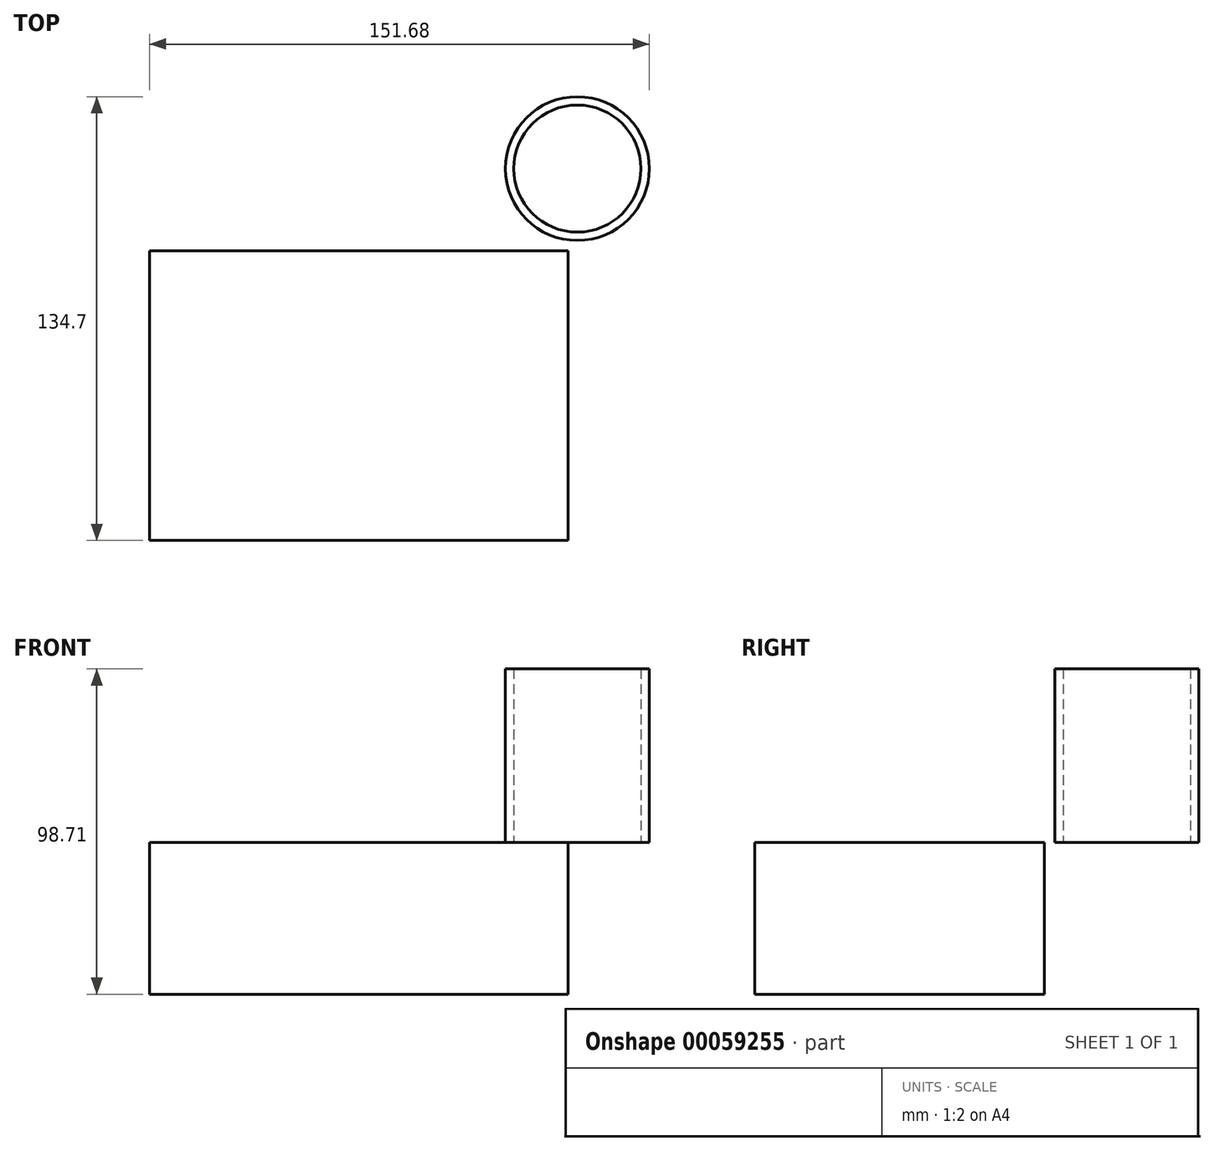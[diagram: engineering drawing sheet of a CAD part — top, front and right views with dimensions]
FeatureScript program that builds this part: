
annotation { "Feature Type Name" : "Feature", "Feature Type Description" : "" }
export const myFeature = defineFeature(function(context is Context, id is Id, definition is map)
    precondition{}
    {
        {
            var Q0;
            Q0=qCreatedBy(makeId("Top.planeOp"),FACE);
            var sketch = newSketch(context, id + "F0", { "sketchPlane" : qUnion([Q0])});
            skLineSegment(sketch, "E0.bottom", {"start": v(-69.6, 48.54) * mm, "end": v(57.4, 48.54) * mm});
            skLineSegment(sketch, "E0.top", {"start": v(-69.6, -39.39) * mm, "end": v(57.4, -39.39) * mm});
            skLineSegment(sketch, "E0.left", {"start": v(-69.6, 48.54) * mm, "end": v(-69.6, -39.39) * mm});
            skLineSegment(sketch, "E0.right", {"start": v(57.4, 48.54) * mm, "end": v(57.4, -39.39) * mm});
            skSolve(sketch);
        }
        {
            var Q0;
            Q0=makeQuery(id+"F0.imprint","IMPRINT",FACE,{"disambiguationData":[TD([[makeQuery(id+"F0.imprint","IMPRINT",EDGE,{"derivedFrom":sQuery(id+"F0.wireOp",EDGE,"E0.bottom")}),-1.0]])]});
            extrude(context, id + "F1", {"entities" : qUnion([Q0]), "oppositeDirection" : true, "depth" : 46.03 * mm});
        }
        {
            var Q0;
            Q0=qCreatedBy(makeId("Top.planeOp"),FACE);
            var sketch = newSketch(context, id + "F2", { "sketchPlane" : qUnion([Q0])});
            skCircle(sketch, "E1", {"center": v(60.26, 73.48) * mm, "radius": 21.83 * mm});
            skSolve(sketch);
        }
        {
            var Q0;
            Q0 = qSketchRegion(id + "F2", true);
            extrude(context, id + "F3", {"entities" : qUnion([Q0]), "depth" : 52.68 * mm});
        }
        {
            var Q0;
            Q0=makeQuery(id+"F3.opExtrude","CAP_FACE",FACE,{"disambiguationData":[OSD([sQuery(id+"F2.wireOp",EDGE,"E1")])],"isStart":false});
            var Q1;
            Q1=makeQuery(id+"F3.opExtrude","CAP_FACE",FACE,{"disambiguationData":[OSD([sQuery(id+"F2.wireOp",EDGE,"E1")])],"isStart":true});
            shell(context, id + "F4", {"entities" : qUnion([Q0, Q1]), "thickness" : 2.54 * mm});
        }
    });
